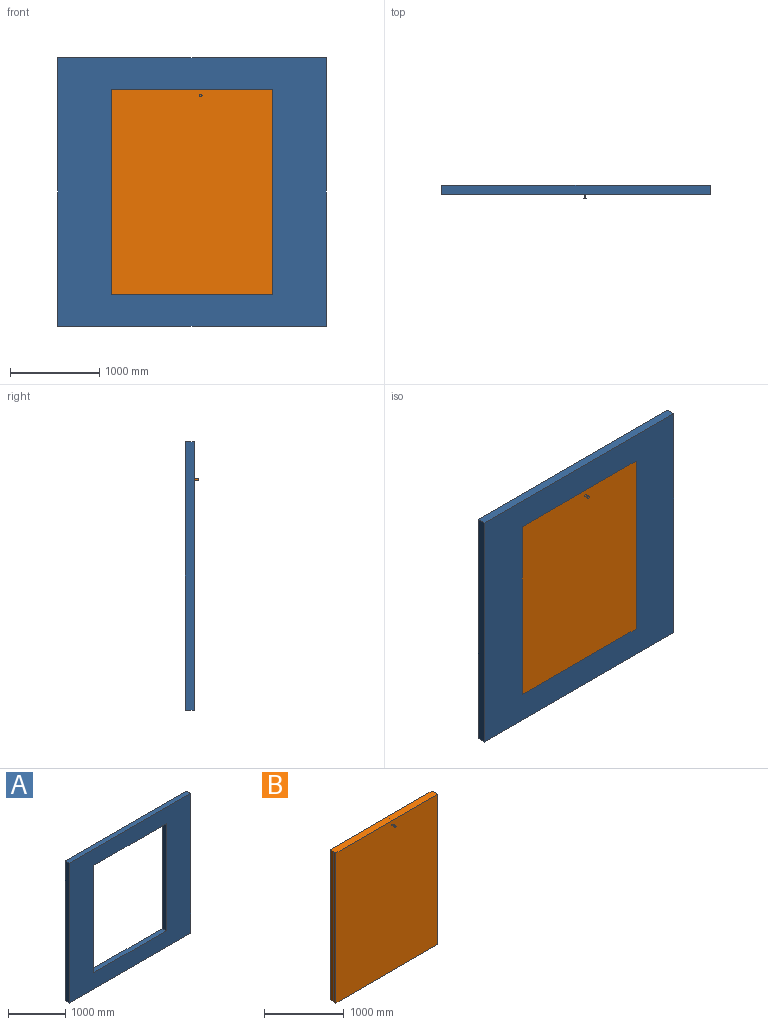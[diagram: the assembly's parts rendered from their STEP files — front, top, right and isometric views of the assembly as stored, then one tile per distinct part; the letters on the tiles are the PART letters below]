
ASSEMBLY  parts=2 mates=1
PART A: 10 faces, bbox 3000x100x3000 mm
  f0: plane 3000x3000mm, normal (0,-1,0), area 4860000mm2, adj f2,f3,f4,f5,f6,f7,f8,f9
  f1: plane 3000x3000mm, normal (0,1,0), area 4860000mm2, adj f2,f3,f4,f5,f6,f7,f8,f9
  f2: plane 3000x100mm, normal (0,0,1), area 300000mm2, adj f0,f1,f3,f5
  f3: plane 3000x100mm, normal (-1,0,0), area 300000mm2, adj f0,f1,f2,f4
  f4: plane 3000x100mm, normal (0,0,-1), area 300000mm2, adj f0,f1,f3,f5
  f5: plane 3000x100mm, normal (1,0,0), area 300000mm2, adj f0,f1,f2,f4
  f6: plane 1800x100mm, normal (0,0,-1), area 180000mm2, adj f0,f1,f7,f9
  f7: plane 2300x100mm, normal (1,0,0), area 230000mm2, adj f0,f1,f6,f8
  f8: plane 1800x100mm, normal (0,0,1), area 180000mm2, adj f0,f1,f7,f9
  f9: plane 2300x100mm, normal (-1,0,0), area 230000mm2, adj f0,f1,f6,f8
PART B: 15 faces, bbox 1800x150x2300 mm
  f0: cylinder r=12.5mm len=50mm, axis (0,1,0), area 1315.4mm2, adj f1,f7,f12,f13
  f1: plane 25x21.71mm, normal (0,-1,0), area 463.4mm2, adj f0,f11,f12,f13
  f2: plane 1800x100mm, normal (0,0,1), area 179992.6mm2, adj f3,f4,f6,f7,f8,f9,f10
  f3: plane 2300x48.75mm, normal (-1,0,0), area 112125mm2, adj f2,f5,f8,f9
  f4: plane 2300x48.75mm, normal (-1,0,0), area 112125mm2, adj f2,f5,f7,f9
  f5: plane 1800x100mm, normal (0,0,-1), area 179992.6mm2, adj f3,f4,f6,f7,f8,f9,f10
  f6: plane 2300x100mm, normal (1,0,0), area 230000mm2, adj f2,f5,f7,f8
  f7: plane 2300x1800mm, normal (0,-1,0), area 4139536.6mm2, adj f0,f2,f4,f5,f6,f11,f12,f13
  f8: plane 2300x1800mm, normal (0,1,0), area 4140000mm2, adj f2,f3,f5,f6
  f9: cylinder r=1.25mm len=2300mm, axis (0,0,1), area 9032.1mm2, adj f2,f3,f4,f5
  f10: cylinder r=1.25mm len=2300mm, axis (0,0,1), area 18064.2mm2, adj f2,f5
  f11: cylinder r=12.5mm len=50mm, axis (0,1,0), area 1315.4mm2, adj f1,f7,f12,f13
  f12: plane 50x12.39mm, normal (0,0,-1), area 506.4mm2, adj f0,f1,f7,f11,f14
  f13: plane 50x12.39mm, normal (0,0,1), area 506.4mm2, adj f0,f1,f7,f11,f14
  f14: cylinder r=6mm len=21.71mm, axis (0,0,1), area 818.6mm2, adj f12,f13
PLACE A t=(-899.96,-418.05,152.32)mm fixed
PLACE B rot(axis=(0,0,-1),0deg) t=(-899.96,-418.05,152.32)mm
MATE revolute B.f9 <-> A.f6  axis (0,0,1) through (-1799.96,-418.05,1302.32)mm
